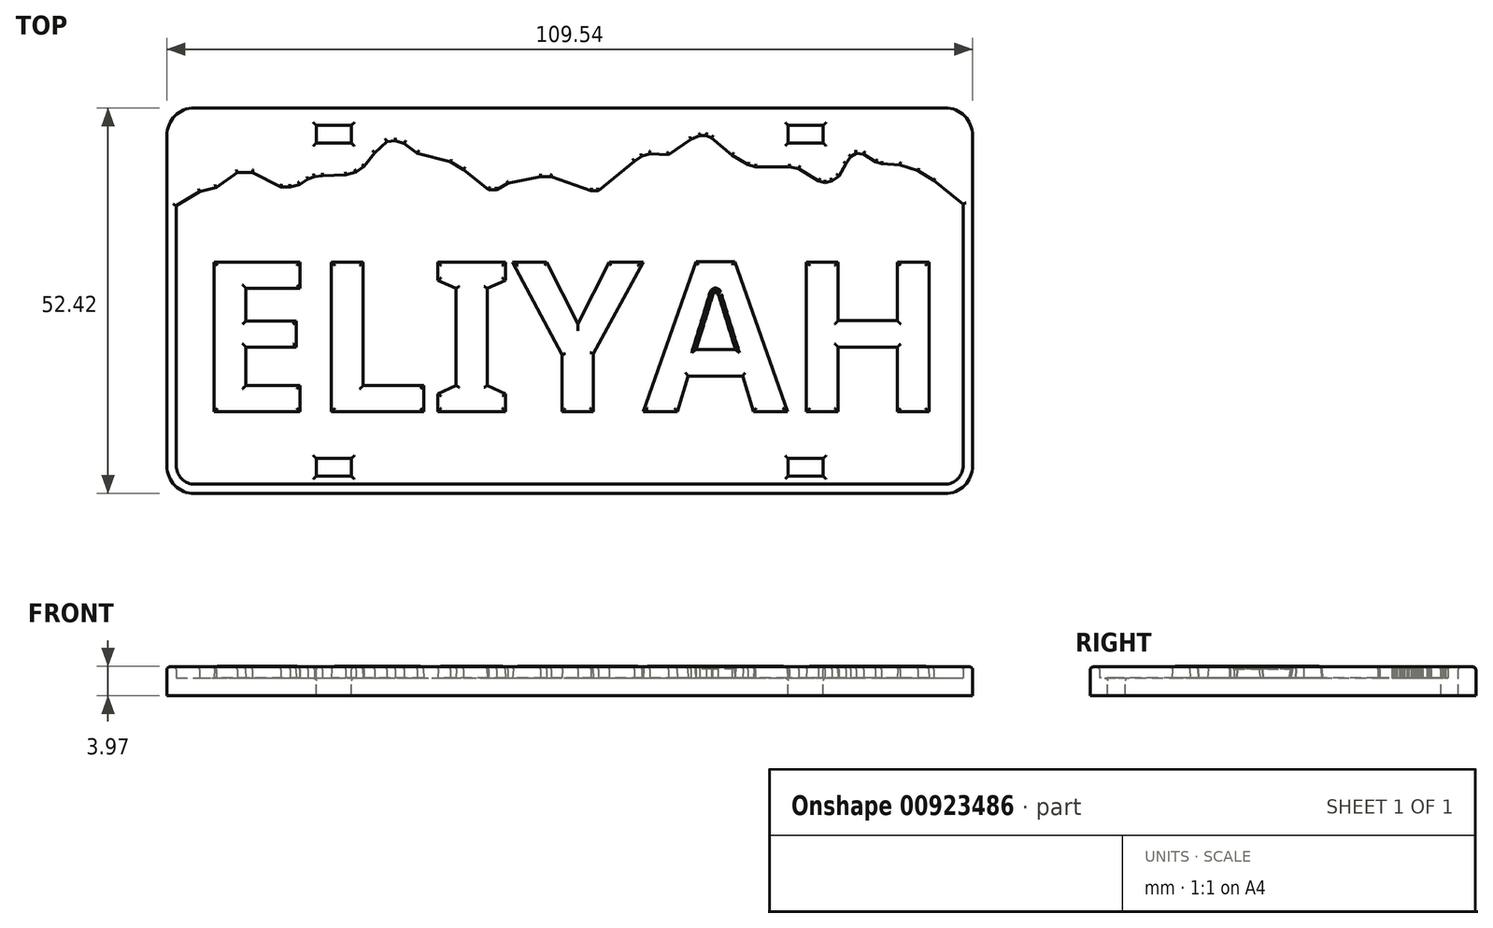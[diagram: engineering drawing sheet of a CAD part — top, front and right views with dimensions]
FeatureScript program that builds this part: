
annotation { "Feature Type Name" : "Feature", "Feature Type Description" : "" }
export const myFeature = defineFeature(function(context is Context, id is Id, definition is map)
    precondition{}
    {
        {
            var Q0;
            Q0=qCreatedBy(makeId("Top.planeOp"),FACE);
            var sketch = newSketch(context, id + "F0", { "sketchPlane" : qUnion([Q0])});
            skLineSegment(sketch, "E0", {"start": v(54.77, -22.46) * mm, "end": v(54.77, 22.46) * mm});
            skArc(sketch, "E1", {"start": v(54.77, 22.46) * mm, "mid": v(53.68, 25.11) * mm, "end": v(51.02, 26.21) * mm});
            skLineSegment(sketch, "E2", {"start": v(51.02, 26.21) * mm, "end": v(-51.02, 26.21) * mm});
            skArc(sketch, "E3", {"start": v(-51.02, 26.21) * mm, "mid": v(-53.68, 25.11) * mm, "end": v(-54.77, 22.46) * mm});
            skLineSegment(sketch, "E4", {"start": v(-54.77, 22.46) * mm, "end": v(-54.77, -22.46) * mm});
            skArc(sketch, "E5", {"start": v(-54.77, -22.46) * mm, "mid": v(-53.54, -25.24) * mm, "end": v(-50.64, -26.2) * mm});
            skLineSegment(sketch, "E6", {"start": v(-50.64, -26.2) * mm, "end": v(51.04, -26.2) * mm});
            skArc(sketch, "E7", {"start": v(51.02, -26.21) * mm, "mid": v(53.68, -25.11) * mm, "end": v(54.77, -22.46) * mm});
            skLineSegment(sketch, "E8", {"start": v(-54.77, 12.13) * mm, "end": v(-50.31, 14.84) * mm});
            skLineSegment(sketch, "E9", {"start": v(-50.31, 14.84) * mm, "end": v(-48.06, 15.4) * mm});
            skLineSegment(sketch, "E10", {"start": v(-48.06, 15.4) * mm, "end": v(-45.2, 17.44) * mm});
            skLineSegment(sketch, "E11", {"start": v(-45.2, 17.44) * mm, "end": v(-43.14, 17.44) * mm});
            skLineSegment(sketch, "E12", {"start": v(-43.14, 17.44) * mm, "end": v(-39.3, 15.5) * mm});
            skLineSegment(sketch, "E13", {"start": v(-39.3, 15.5) * mm, "end": v(-38.03, 15.49) * mm});
            skLineSegment(sketch, "E14", {"start": v(-38.03, 15.49) * mm, "end": v(-36.75, 15.8) * mm});
            skLineSegment(sketch, "E15", {"start": v(-36.75, 15.8) * mm, "end": v(-35.57, 16.54) * mm});
            skLineSegment(sketch, "E16", {"start": v(-35.57, 16.54) * mm, "end": v(-34.73, 16.88) * mm});
            skLineSegment(sketch, "E17", {"start": v(-34.73, 16.88) * mm, "end": v(-33.6, 17.01) * mm});
            skLineSegment(sketch, "E18", {"start": v(-33.6, 17.01) * mm, "end": v(-30.43, 17.11) * mm});
            skLineSegment(sketch, "E19", {"start": v(-29.05, 17.5) * mm, "end": v(-27.98, 18.27) * mm});
            skLineSegment(sketch, "E20", {"start": v(-27.98, 18.27) * mm, "end": v(-26.53, 20.14) * mm});
            skLineSegment(sketch, "E21", {"start": v(-26.53, 20.14) * mm, "end": v(-24.88, 21.63) * mm});
            skLineSegment(sketch, "E22", {"start": v(-24.88, 21.63) * mm, "end": v(-23.73, 21.77) * mm});
            skLineSegment(sketch, "E23", {"start": v(-22.5, 21.4) * mm, "end": v(-20.72, 20.04) * mm});
            skLineSegment(sketch, "E24", {"start": v(-16.23, 18.87) * mm, "end": v(-14.45, 17.85) * mm});
            skLineSegment(sketch, "E25", {"start": v(-14.45, 17.85) * mm, "end": v(-11.02, 15.1) * mm});
            skLineSegment(sketch, "E26", {"start": v(-11.02, 15.1) * mm, "end": v(-9.93, 15.1) * mm});
            skLineSegment(sketch, "E27", {"start": v(-9.93, 15.1) * mm, "end": v(-8.4, 15.96) * mm});
            skLineSegment(sketch, "E28", {"start": v(-8.4, 15.96) * mm, "end": v(-3.94, 16.85) * mm});
            skLineSegment(sketch, "E29", {"start": v(-3.94, 16.85) * mm, "end": v(-2.54, 16.85) * mm});
            skLineSegment(sketch, "E30", {"start": v(-2.54, 16.85) * mm, "end": v(2.9, 14.97) * mm});
            skLineSegment(sketch, "E31", {"start": v(2.9, 14.97) * mm, "end": v(3.92, 14.97) * mm});
            skLineSegment(sketch, "E32", {"start": v(3.92, 14.97) * mm, "end": v(8.8, 18.97) * mm});
            skLineSegment(sketch, "E33", {"start": v(8.8, 18.97) * mm, "end": v(9.82, 19.64) * mm});
            skLineSegment(sketch, "E34", {"start": v(9.82, 19.64) * mm, "end": v(10.9, 19.97) * mm});
            skLineSegment(sketch, "E35", {"start": v(10.9, 19.97) * mm, "end": v(13.43, 19.86) * mm});
            skLineSegment(sketch, "E36", {"start": v(16.5, 21.96) * mm, "end": v(17.71, 22.42) * mm});
            skLineSegment(sketch, "E37", {"start": v(17.71, 22.42) * mm, "end": v(18.56, 22.45) * mm});
            skLineSegment(sketch, "E38", {"start": v(18.56, 22.45) * mm, "end": v(19.28, 22.13) * mm});
            skLineSegment(sketch, "E39", {"start": v(19.28, 22.13) * mm, "end": v(22.05, 19.8) * mm});
            skLineSegment(sketch, "E40", {"start": v(22.05, 19.8) * mm, "end": v(24.2, 18.5) * mm});
            skLineSegment(sketch, "E41", {"start": v(24.2, 18.5) * mm, "end": v(25.23, 18.2) * mm});
            skLineSegment(sketch, "E42", {"start": v(25.23, 18.2) * mm, "end": v(29.85, 18.2) * mm});
            skLineSegment(sketch, "E43", {"start": v(29.85, 18.2) * mm, "end": v(31.13, 17.95) * mm});
            skLineSegment(sketch, "E44", {"start": v(31.13, 17.95) * mm, "end": v(33.84, 16.27) * mm});
            skLineSegment(sketch, "E45", {"start": v(33.84, 16.27) * mm, "end": v(34.73, 16.06) * mm});
            skLineSegment(sketch, "E46", {"start": v(34.73, 16.06) * mm, "end": v(35.67, 16.3) * mm});
            skLineSegment(sketch, "E47", {"start": v(35.67, 16.3) * mm, "end": v(36.58, 16.95) * mm});
            skLineSegment(sketch, "E48", {"start": v(36.58, 16.95) * mm, "end": v(37.58, 18.67) * mm});
            skLineSegment(sketch, "E49", {"start": v(38.22, 19.58) * mm, "end": v(38.96, 20.06) * mm});
            skLineSegment(sketch, "E50", {"start": v(38.96, 20.06) * mm, "end": v(39.94, 19.92) * mm});
            skLineSegment(sketch, "E51", {"start": v(41.58, 18.88) * mm, "end": v(42.4, 18.61) * mm});
            skLineSegment(sketch, "E52", {"start": v(42.4, 18.61) * mm, "end": v(44.9, 18.47) * mm});
            skLineSegment(sketch, "E53", {"start": v(44.9, 18.47) * mm, "end": v(47.31, 17.68) * mm});
            skLineSegment(sketch, "E54", {"start": v(47.31, 17.68) * mm, "end": v(49.47, 16.33) * mm});
            skLineSegment(sketch, "E55", {"start": v(49.47, 16.33) * mm, "end": v(51.88, 14.42) * mm});
            skLineSegment(sketch, "E56", {"start": v(51.88, 14.42) * mm, "end": v(53.78, 12.92) * mm});
            skLineSegment(sketch, "E57", {"start": v(53.78, 12.92) * mm, "end": v(54.77, 12.06) * mm});
            skLineSegment(sketch, "E58", {"start": v(-20.72, 20.04) * mm, "end": v(-16.23, 18.87) * mm});
            skLineSegment(sketch, "E59", {"start": v(16.5, 21.96) * mm, "end": v(13.43, 19.86) * mm});
            skLineSegment(sketch, "E60", {"start": v(-22.5, 21.4) * mm, "end": v(-23.73, 21.77) * mm});
            skLineSegment(sketch, "E61", {"start": v(-29.05, 17.5) * mm, "end": v(-30.43, 17.11) * mm});
            skLineSegment(sketch, "E62", {"start": v(37.58, 18.67) * mm, "end": v(38.22, 19.58) * mm});
            skLineSegment(sketch, "E63", {"start": v(41.58, 18.88) * mm, "end": v(39.94, 19.92) * mm});
            skSolve(sketch);
        }
        {
            var Q0;
            Q0=qCreatedBy(makeId("Top.planeOp"),FACE);
            var sketch = newSketch(context, id + "F1", { "sketchPlane" : qUnion([Q0])});
            skLineSegment(sketch, "E64", {"start": v(54.77, -22.46) * mm, "end": v(54.77, 22.46) * mm});
            skArc(sketch, "E65", {"start": v(54.77, 22.46) * mm, "mid": v(53.68, 25.11) * mm, "end": v(51.02, 26.21) * mm});
            skLineSegment(sketch, "E66", {"start": v(51.02, 26.21) * mm, "end": v(-51.02, 26.21) * mm});
            skArc(sketch, "E67", {"start": v(-51.02, 26.21) * mm, "mid": v(-53.68, 25.11) * mm, "end": v(-54.77, 22.46) * mm});
            skLineSegment(sketch, "E68", {"start": v(-54.77, 22.46) * mm, "end": v(-54.77, -22.46) * mm});
            skArc(sketch, "E69", {"start": v(-54.77, -22.46) * mm, "mid": v(-53.68, -25.11) * mm, "end": v(-51.02, -26.21) * mm});
            skLineSegment(sketch, "E70", {"start": v(-51.02, -26.21) * mm, "end": v(51.02, -26.21) * mm});
            skArc(sketch, "E71", {"start": v(51.02, -26.21) * mm, "mid": v(53.68, -25.11) * mm, "end": v(54.77, -22.46) * mm});
            skLineSegment(sketch, "E72.0", {"start": v(50.96, 24.94) * mm, "end": v(-50.96, 24.94) * mm, "construction": true});
            skLineSegment(sketch, "E72.1", {"start": v(53.5, -22.4) * mm, "end": v(53.5, 22.4) * mm, "construction": true});
            skLineSegment(sketch, "E72.2", {"start": v(-50.96, -24.94) * mm, "end": v(50.96, -24.94) * mm, "construction": true});
            skLineSegment(sketch, "E72.3", {"start": v(-53.5, 22.4) * mm, "end": v(-53.5, -22.4) * mm, "construction": true});
            skPoint(sketch, "E73.visualSharp", {"position": v(-53.5, 24.94) * mm});
            skArc(sketch, "E73.filletArc", {"start": v(-50.96, 24.94) * mm, "mid": v(-52.76, 24.2) * mm, "end": v(-53.5, 22.4) * mm, "construction": true});
            skPoint(sketch, "E74.visualSharp", {"position": v(-53.5, -24.94) * mm});
            skArc(sketch, "E74.filletArc", {"start": v(-53.5, -22.4) * mm, "mid": v(-52.76, -24.2) * mm, "end": v(-50.96, -24.94) * mm, "construction": true});
            skPoint(sketch, "E75.visualSharp", {"position": v(53.5, -24.94) * mm});
            skArc(sketch, "E75.filletArc", {"start": v(50.96, -24.94) * mm, "mid": v(52.76, -24.2) * mm, "end": v(53.5, -22.4) * mm, "construction": true});
            skPoint(sketch, "E76.visualSharp", {"position": v(53.5, 24.94) * mm});
            skArc(sketch, "E76.filletArc", {"start": v(53.5, 22.4) * mm, "mid": v(52.76, 24.2) * mm, "end": v(50.96, 24.94) * mm, "construction": true});
            skSolve(sketch);
        }
        {
            var Q0;
            {var subQ3=sQuery(id+"F0.wireOp",EDGE,"E1");Q0=makeQuery(id+"F0.imprint","IMPRINT",FACE,{"disambiguationData":[TD([[makeQuery(id+"F0.imprint","IMPRINT",EDGE,{"derivedFrom":subQ3}),1.0]])]});}
            extrude(context, id + "F2", {"entities" : qUnion([Q0]), "depth" : 1.52 * mm, "offsetDistance" : 25.4 * mm});
        }
        {
            var Q0;
            Q0=qSketchRegion(id+"F1",true);
            extrude(context, id + "F3", {"entities" : qUnion([Q0]), "operationType" : NewBodyOperationType.ADD, "oppositeDirection" : true, "depth" : 2.38 * mm, "offsetDistance" : 25.4 * mm});
        }
        {
            var Q0;
            {var subQ58=sQuery(id+"F0.wireOp",EDGE,"E0");var subQ59=sQuery(id+"F1.wireOp",EDGE,"E64");var subQ60=sQuery(id+"F1.wireOp",EDGE,"E65");var subQ61=sQuery(id+"F1.wireOp",EDGE,"E68");var subQ62=sQuery(id+"F1.wireOp",EDGE,"E69");var subQ63=sQuery(id+"F1.wireOp",EDGE,"E70");var subQ64=sQuery(id+"F1.wireOp",EDGE,"E71");Q0=makeQuery(id+"F3.boolean.opBoolean","SPLIT",FACE,{"disambiguationData":[TD([makeQuery(id+"F2.opExtrude","SWEPT_FACE",FACE,{"disambiguationData":[OSD([subQ58])]})])],"derivedFrom":makeQuery(id+"F3.opExtrude","CAP_FACE",FACE,{"disambiguationData":[OSD([subQ59,subQ60,sQuery(id+"F1.wireOp",EDGE,"E66"),sQuery(id+"F1.wireOp",EDGE,"E67"),subQ61,subQ62,subQ63,subQ64])],"isStart":true})});}
            var sketch = newSketch(context, id + "F4", { "sketchPlane" : qUnion([Q0])});
            skLineSegment(sketch, "E77", {"start": v(54.77, -22.46) * mm, "end": v(54.77, 12.06) * mm});
            skLineSegment(sketch, "E78", {"start": v(-54.77, 12.13) * mm, "end": v(-54.77, -22.46) * mm});
            skArc(sketch, "E79", {"start": v(-54.77, -22.46) * mm, "mid": v(-53.68, -25.11) * mm, "end": v(-51.02, -26.21) * mm});
            skLineSegment(sketch, "E80", {"start": v(-51.02, -26.21) * mm, "end": v(51.02, -26.21) * mm});
            skArc(sketch, "E81", {"start": v(51.02, -26.21) * mm, "mid": v(53.68, -25.11) * mm, "end": v(54.77, -22.46) * mm});
            skLineSegment(sketch, "E82.1", {"start": v(53.5, -22.4) * mm, "end": v(53.5, 13.14) * mm});
            skLineSegment(sketch, "E82.2", {"start": v(-50.96, -24.94) * mm, "end": v(50.96, -24.94) * mm});
            skLineSegment(sketch, "E82.3", {"start": v(-53.5, 12.9) * mm, "end": v(-53.5, -22.4) * mm});
            skPoint(sketch, "E83.visualSharp", {"position": v(-53.5, 24.94) * mm});
            skPoint(sketch, "E84.visualSharp", {"position": v(-53.5, -24.94) * mm});
            skArc(sketch, "E84.filletArc", {"start": v(-53.5, -22.4) * mm, "mid": v(-52.76, -24.2) * mm, "end": v(-50.96, -24.94) * mm});
            skPoint(sketch, "E85.visualSharp", {"position": v(53.5, -24.94) * mm});
            skArc(sketch, "E85.filletArc", {"start": v(50.96, -24.94) * mm, "mid": v(52.76, -24.2) * mm, "end": v(53.5, -22.4) * mm});
            skPoint(sketch, "E86.visualSharp", {"position": v(53.5, 24.94) * mm});
            skLineSegment(sketch, "E87", {"start": v(-54.77, 12.13) * mm, "end": v(-53.5, 12.9) * mm});
            skLineSegment(sketch, "E88", {"start": v(53.5, 13.14) * mm, "end": v(53.78, 12.92) * mm});
            skLineSegment(sketch, "E89", {"start": v(53.78, 12.92) * mm, "end": v(54.77, 12.06) * mm});
            skSolve(sketch);
        }
        {
            var Q0;
            Q0=qSketchRegion(id+"F4",true);
            extrude(context, id + "F5", {"entities" : qUnion([Q0]), "operationType" : NewBodyOperationType.ADD, "depth" : 1.52 * mm, "offsetDistance" : 25.4 * mm});
        }
        {
            var Q0;
            Q0=makeQuery(id+"F5.boolean.opBoolean","MERGE",FACE,{"derivedFrom":[makeQuery(id+"F2.opExtrude","CAP_FACE",FACE,{"disambiguationData":[OSD([sQuery(id+"F0.wireOp",EDGE,"E0"),sQuery(id+"F0.wireOp",EDGE,"E1"),sQuery(id+"F0.wireOp",EDGE,"E2"),sQuery(id+"F0.wireOp",EDGE,"E3"),sQuery(id+"F0.wireOp",EDGE,"E4"),sQuery(id+"F0.wireOp",EDGE,"E8"),sQuery(id+"F0.wireOp",EDGE,"E9"),sQuery(id+"F0.wireOp",EDGE,"E10"),sQuery(id+"F0.wireOp",EDGE,"E11"),sQuery(id+"F0.wireOp",EDGE,"E12"),sQuery(id+"F0.wireOp",EDGE,"E13"),sQuery(id+"F0.wireOp",EDGE,"E14"),sQuery(id+"F0.wireOp",EDGE,"E15"),sQuery(id+"F0.wireOp",EDGE,"E16"),sQuery(id+"F0.wireOp",EDGE,"E17"),sQuery(id+"F0.wireOp",EDGE,"E18"),sQuery(id+"F0.wireOp",EDGE,"7b9f405e-0691-426e-9c9e-a5372cf0836a"),sQuery(id+"F0.wireOp",EDGE,"E19"),sQuery(id+"F0.wireOp",EDGE,"E20"),sQuery(id+"F0.wireOp",EDGE,"E21"),sQuery(id+"F0.wireOp",EDGE,"E22"),sQuery(id+"F0.wireOp",EDGE,"b3dec5b1-662c-4d50-a13c-af7b7760114a"),sQuery(id+"F0.wireOp",EDGE,"E23"),sQuery(id+"F0.wireOp",EDGE,"4d9ee76e-0833-4cdc-b1a8-2d4ce76e6521"),sQuery(id+"F0.wireOp",EDGE,"E24"),sQuery(id+"F0.wireOp",EDGE,"E25"),sQuery(id+"F0.wireOp",EDGE,"E26"),sQuery(id+"F0.wireOp",EDGE,"E27"),sQuery(id+"F0.wireOp",EDGE,"E28"),sQuery(id+"F0.wireOp",EDGE,"E29"),sQuery(id+"F0.wireOp",EDGE,"E30"),sQuery(id+"F0.wireOp",EDGE,"E31"),sQuery(id+"F0.wireOp",EDGE,"E32"),sQuery(id+"F0.wireOp",EDGE,"E33"),sQuery(id+"F0.wireOp",EDGE,"E34"),sQuery(id+"F0.wireOp",EDGE,"E35"),sQuery(id+"F0.wireOp",EDGE,"55551997-bb9e-4b94-90c5-def3cb147476"),sQuery(id+"F0.wireOp",EDGE,"E36"),sQuery(id+"F0.wireOp",EDGE,"E37"),sQuery(id+"F0.wireOp",EDGE,"E38"),sQuery(id+"F0.wireOp",EDGE,"E39"),sQuery(id+"F0.wireOp",EDGE,"E40"),sQuery(id+"F0.wireOp",EDGE,"E41"),sQuery(id+"F0.wireOp",EDGE,"E42"),sQuery(id+"F0.wireOp",EDGE,"E43"),sQuery(id+"F0.wireOp",EDGE,"E44"),sQuery(id+"F0.wireOp",EDGE,"E45"),sQuery(id+"F0.wireOp",EDGE,"E46"),sQuery(id+"F0.wireOp",EDGE,"E47"),sQuery(id+"F0.wireOp",EDGE,"E48"),sQuery(id+"F0.wireOp",EDGE,"513b7cbe-d979-4e22-b277-f3c42ccdbda1"),sQuery(id+"F0.wireOp",EDGE,"E49"),sQuery(id+"F0.wireOp",EDGE,"E50"),sQuery(id+"F0.wireOp",EDGE,"0d842e13-672c-40e3-aae4-28923e78d4e0"),sQuery(id+"F0.wireOp",EDGE,"E51"),sQuery(id+"F0.wireOp",EDGE,"E52"),sQuery(id+"F0.wireOp",EDGE,"E53"),sQuery(id+"F0.wireOp",EDGE,"E54"),sQuery(id+"F0.wireOp",EDGE,"E55"),sQuery(id+"F0.wireOp",EDGE,"E56"),sQuery(id+"F0.wireOp",EDGE,"E57")])],"isStart":false}),makeQuery(id+"F5.opExtrude","CAP_FACE",FACE,{"disambiguationData":[OSD([sQuery(id+"F4.wireOp",EDGE,"E77"),sQuery(id+"F4.wireOp",EDGE,"E78"),sQuery(id+"F4.wireOp",EDGE,"E79"),sQuery(id+"F4.wireOp",EDGE,"E80"),sQuery(id+"F4.wireOp",EDGE,"E81"),sQuery(id+"F4.wireOp",EDGE,"E82.1"),sQuery(id+"F4.wireOp",EDGE,"E82.2"),sQuery(id+"F4.wireOp",EDGE,"E82.3"),sQuery(id+"F4.wireOp",EDGE,"E84.filletArc"),sQuery(id+"F4.wireOp",EDGE,"E85.filletArc"),sQuery(id+"F4.wireOp",EDGE,"E87"),sQuery(id+"F4.wireOp",EDGE,"E88"),sQuery(id+"F4.wireOp",EDGE,"E89")])],"isStart":false})]});
            var sketch = newSketch(context, id + "F6", { "sketchPlane" : qUnion([Q0])});
            skLineSegment(sketch, "E90.bottom", {"start": v(-34.45, 23.83) * mm, "end": v(-29.7, 23.83) * mm});
            skLineSegment(sketch, "E90.top", {"start": v(-34.45, 21.45) * mm, "end": v(-29.7, 21.45) * mm});
            skLineSegment(sketch, "E90.left", {"start": v(-34.45, 23.83) * mm, "end": v(-34.45, 21.45) * mm});
            skLineSegment(sketch, "E90.right", {"start": v(-29.7, 23.83) * mm, "end": v(-29.7, 21.45) * mm});
            skLineSegment(sketch, "E91", {"start": v(0, 26.21) * mm, "end": v(0, -26.21) * mm, "construction": true});
            skLineSegment(sketch, "E92.MirrorCS", {"start": v(34.45, 23.83) * mm, "end": v(34.45, 21.45) * mm});
            skLineSegment(sketch, "E93.MirrorCS", {"start": v(29.7, 23.83) * mm, "end": v(29.7, 21.45) * mm});
            skLineSegment(sketch, "E94.MirrorCS", {"start": v(34.45, 21.45) * mm, "end": v(29.7, 21.45) * mm});
            skLineSegment(sketch, "E95.MirrorCS", {"start": v(34.45, 23.83) * mm, "end": v(29.7, 23.83) * mm});
            skLineSegment(sketch, "E96", {"start": v(0, 0) * mm, "end": v(-59.23, 0) * mm, "construction": true});
            skLineSegment(sketch, "E97", {"start": v(0, 0) * mm, "end": v(56.47, 0) * mm, "construction": true});
            skLineSegment(sketch, "E98.MirrorCS", {"start": v(-34.45, -23.83) * mm, "end": v(-29.7, -23.83) * mm});
            skLineSegment(sketch, "E99.MirrorCS", {"start": v(-34.45, -23.83) * mm, "end": v(-34.45, -21.45) * mm});
            skLineSegment(sketch, "E100.MirrorCS", {"start": v(-34.45, -21.45) * mm, "end": v(-29.7, -21.45) * mm});
            skLineSegment(sketch, "E101.MirrorCS", {"start": v(-29.7, -23.83) * mm, "end": v(-29.7, -21.45) * mm});
            skLineSegment(sketch, "E102.MirrorCS", {"start": v(29.7, -23.83) * mm, "end": v(29.7, -21.45) * mm});
            skLineSegment(sketch, "E103.MirrorCS", {"start": v(34.45, -23.83) * mm, "end": v(29.7, -23.83) * mm});
            skLineSegment(sketch, "E104.MirrorCS", {"start": v(34.45, -23.83) * mm, "end": v(34.45, -21.45) * mm});
            skLineSegment(sketch, "E105.MirrorCS", {"start": v(34.45, -21.45) * mm, "end": v(29.7, -21.45) * mm});
            skSolve(sketch);
        }
        {
            var Q0;
            Q0=qSketchRegion(id+"F6",true);
            extrude(context, id + "F7", {"entities" : qUnion([Q0]), "operationType" : NewBodyOperationType.REMOVE, "endBound" : BoundingType.THROUGH_ALL, "oppositeDirection" : true, "depth" : 25.4 * mm, "offsetDistance" : 25.4 * mm});
        }
        {
            var Q0;
            Q0=makeQuery(id+"F3.opExtrude","CAP_FACE",FACE,{"disambiguationData":[OSD([sQuery(id+"F1.wireOp",EDGE,"E64"),sQuery(id+"F1.wireOp",EDGE,"E65"),sQuery(id+"F1.wireOp",EDGE,"E66"),sQuery(id+"F1.wireOp",EDGE,"E67"),sQuery(id+"F1.wireOp",EDGE,"E68"),sQuery(id+"F1.wireOp",EDGE,"E69"),sQuery(id+"F1.wireOp",EDGE,"E70"),sQuery(id+"F1.wireOp",EDGE,"E71")])],"isStart":true});
            var sketch = newSketch(context, id + "F8", { "sketchPlane" : qUnion([Q0])});
            skText(sketch, "E106", { "text": "ELIYAH", "fontName": "NotoSans-Bold.ttf"});
            const initialGuessF8  = {"E106": [-0.0509, -0.01508, 1, 0, 0.0205]};
            skSetInitialGuess(sketch, initialGuessF8);
            skSolve(sketch);
        }
        {
            var Q0;
            Q0=qSketchRegion(id+"F8",true);
            extrude(context, id + "F9", {"entities" : qUnion([Q0]), "operationType" : NewBodyOperationType.ADD, "depth" : 1.59 * mm, "offsetDistance" : 25.4 * mm, "hasDraft" : true, "draftAngle" : 3 * degree, "draftPullDirection" : true});
        }
        {
            var Q0;
            Q0=makeQuery(id+"F5.boolean.opBoolean","MERGE",FACE,{"derivedFrom":[makeQuery(id+"F2.opExtrude","CAP_FACE",FACE,{"disambiguationData":[OSD([sQuery(id+"F0.wireOp",EDGE,"E0"),sQuery(id+"F0.wireOp",EDGE,"E1"),sQuery(id+"F0.wireOp",EDGE,"E2"),sQuery(id+"F0.wireOp",EDGE,"E3"),sQuery(id+"F0.wireOp",EDGE,"E4"),sQuery(id+"F0.wireOp",EDGE,"E8"),sQuery(id+"F0.wireOp",EDGE,"E9"),sQuery(id+"F0.wireOp",EDGE,"E10"),sQuery(id+"F0.wireOp",EDGE,"E11"),sQuery(id+"F0.wireOp",EDGE,"E12"),sQuery(id+"F0.wireOp",EDGE,"E13"),sQuery(id+"F0.wireOp",EDGE,"E14"),sQuery(id+"F0.wireOp",EDGE,"E15"),sQuery(id+"F0.wireOp",EDGE,"E16"),sQuery(id+"F0.wireOp",EDGE,"E17"),sQuery(id+"F0.wireOp",EDGE,"E18"),sQuery(id+"F0.wireOp",EDGE,"7b9f405e-0691-426e-9c9e-a5372cf0836a"),sQuery(id+"F0.wireOp",EDGE,"E19"),sQuery(id+"F0.wireOp",EDGE,"E20"),sQuery(id+"F0.wireOp",EDGE,"E21"),sQuery(id+"F0.wireOp",EDGE,"E22"),sQuery(id+"F0.wireOp",EDGE,"b3dec5b1-662c-4d50-a13c-af7b7760114a"),sQuery(id+"F0.wireOp",EDGE,"E23"),sQuery(id+"F0.wireOp",EDGE,"4d9ee76e-0833-4cdc-b1a8-2d4ce76e6521"),sQuery(id+"F0.wireOp",EDGE,"E24"),sQuery(id+"F0.wireOp",EDGE,"E25"),sQuery(id+"F0.wireOp",EDGE,"E26"),sQuery(id+"F0.wireOp",EDGE,"E27"),sQuery(id+"F0.wireOp",EDGE,"E28"),sQuery(id+"F0.wireOp",EDGE,"E29"),sQuery(id+"F0.wireOp",EDGE,"E30"),sQuery(id+"F0.wireOp",EDGE,"E31"),sQuery(id+"F0.wireOp",EDGE,"E32"),sQuery(id+"F0.wireOp",EDGE,"E33"),sQuery(id+"F0.wireOp",EDGE,"E34"),sQuery(id+"F0.wireOp",EDGE,"E35"),sQuery(id+"F0.wireOp",EDGE,"55551997-bb9e-4b94-90c5-def3cb147476"),sQuery(id+"F0.wireOp",EDGE,"E36"),sQuery(id+"F0.wireOp",EDGE,"E37"),sQuery(id+"F0.wireOp",EDGE,"E38"),sQuery(id+"F0.wireOp",EDGE,"E39"),sQuery(id+"F0.wireOp",EDGE,"E40"),sQuery(id+"F0.wireOp",EDGE,"E41"),sQuery(id+"F0.wireOp",EDGE,"E42"),sQuery(id+"F0.wireOp",EDGE,"E43"),sQuery(id+"F0.wireOp",EDGE,"E44"),sQuery(id+"F0.wireOp",EDGE,"E45"),sQuery(id+"F0.wireOp",EDGE,"E46"),sQuery(id+"F0.wireOp",EDGE,"E47"),sQuery(id+"F0.wireOp",EDGE,"E48"),sQuery(id+"F0.wireOp",EDGE,"513b7cbe-d979-4e22-b277-f3c42ccdbda1"),sQuery(id+"F0.wireOp",EDGE,"E49"),sQuery(id+"F0.wireOp",EDGE,"E50"),sQuery(id+"F0.wireOp",EDGE,"0d842e13-672c-40e3-aae4-28923e78d4e0"),sQuery(id+"F0.wireOp",EDGE,"E51"),sQuery(id+"F0.wireOp",EDGE,"E52"),sQuery(id+"F0.wireOp",EDGE,"E53"),sQuery(id+"F0.wireOp",EDGE,"E54"),sQuery(id+"F0.wireOp",EDGE,"E55"),sQuery(id+"F0.wireOp",EDGE,"E56"),sQuery(id+"F0.wireOp",EDGE,"E57")])],"isStart":false}),makeQuery(id+"F5.opExtrude","CAP_FACE",FACE,{"disambiguationData":[OSD([sQuery(id+"F4.wireOp",EDGE,"E77"),sQuery(id+"F4.wireOp",EDGE,"E78"),sQuery(id+"F4.wireOp",EDGE,"E79"),sQuery(id+"F4.wireOp",EDGE,"E80"),sQuery(id+"F4.wireOp",EDGE,"E81"),sQuery(id+"F4.wireOp",EDGE,"E82.1"),sQuery(id+"F4.wireOp",EDGE,"E82.2"),sQuery(id+"F4.wireOp",EDGE,"E82.3"),sQuery(id+"F4.wireOp",EDGE,"E84.filletArc"),sQuery(id+"F4.wireOp",EDGE,"E85.filletArc"),sQuery(id+"F4.wireOp",EDGE,"E87"),sQuery(id+"F4.wireOp",EDGE,"E88"),sQuery(id+"F4.wireOp",EDGE,"E89")])],"isStart":false})]});
            var Q1;
            {var subQ0=sQuery(id+"F1.wireOp",EDGE,"E64");var subQ1=sQuery(id+"F1.wireOp",EDGE,"E68");var subQ2=sQuery(id+"F1.wireOp",EDGE,"E69");var subQ3=sQuery(id+"F1.wireOp",EDGE,"E70");var subQ4=sQuery(id+"F1.wireOp",EDGE,"E71");Q1=makeQuery(id+"F7.boolean.opBoolean","INTERSECT",EDGE,{"derivedFrom":[makeQuery(id+"F3.boolean.opBoolean","SPLIT",FACE,{"disambiguationData":[TD([makeQuery(id+"F2.opExtrude","SWEPT_FACE",FACE,{"disambiguationData":[OSD([sQuery(id+"F0.wireOp",EDGE,"E0")])]})])],"derivedFrom":makeQuery(id+"F3.opExtrude","CAP_FACE",FACE,{"disambiguationData":[OSD([subQ0,sQuery(id+"F1.wireOp",EDGE,"E65"),sQuery(id+"F1.wireOp",EDGE,"E66"),sQuery(id+"F1.wireOp",EDGE,"E67"),subQ1,subQ2,subQ3,subQ4])],"isStart":true})}),makeQuery(id+"F7.opExtrude","SWEPT_FACE",FACE,{"disambiguationData":[OSD([sQuery(id+"F6.wireOp",EDGE,"E100.MirrorCS")])]})]});}
            var Q2;
            {var subQ0=sQuery(id+"F1.wireOp",EDGE,"E64");var subQ1=sQuery(id+"F1.wireOp",EDGE,"E68");var subQ2=sQuery(id+"F1.wireOp",EDGE,"E69");var subQ3=sQuery(id+"F1.wireOp",EDGE,"E70");var subQ4=sQuery(id+"F1.wireOp",EDGE,"E71");Q2=makeQuery(id+"F7.boolean.opBoolean","INTERSECT",EDGE,{"derivedFrom":[makeQuery(id+"F3.boolean.opBoolean","SPLIT",FACE,{"disambiguationData":[TD([makeQuery(id+"F2.opExtrude","SWEPT_FACE",FACE,{"disambiguationData":[OSD([sQuery(id+"F0.wireOp",EDGE,"E0")])]})])],"derivedFrom":makeQuery(id+"F3.opExtrude","CAP_FACE",FACE,{"disambiguationData":[OSD([subQ0,sQuery(id+"F1.wireOp",EDGE,"E65"),sQuery(id+"F1.wireOp",EDGE,"E66"),sQuery(id+"F1.wireOp",EDGE,"E67"),subQ1,subQ2,subQ3,subQ4])],"isStart":true})}),makeQuery(id+"F7.opExtrude","SWEPT_FACE",FACE,{"disambiguationData":[OSD([sQuery(id+"F6.wireOp",EDGE,"E99.MirrorCS")])]})]});}
            var Q3;
            {var subQ0=sQuery(id+"F1.wireOp",EDGE,"E64");var subQ1=sQuery(id+"F1.wireOp",EDGE,"E68");var subQ2=sQuery(id+"F1.wireOp",EDGE,"E69");var subQ3=sQuery(id+"F1.wireOp",EDGE,"E70");var subQ4=sQuery(id+"F1.wireOp",EDGE,"E71");Q3=makeQuery(id+"F7.boolean.opBoolean","INTERSECT",EDGE,{"derivedFrom":[makeQuery(id+"F3.boolean.opBoolean","SPLIT",FACE,{"disambiguationData":[TD([makeQuery(id+"F2.opExtrude","SWEPT_FACE",FACE,{"disambiguationData":[OSD([sQuery(id+"F0.wireOp",EDGE,"E0")])]})])],"derivedFrom":makeQuery(id+"F3.opExtrude","CAP_FACE",FACE,{"disambiguationData":[OSD([subQ0,sQuery(id+"F1.wireOp",EDGE,"E65"),sQuery(id+"F1.wireOp",EDGE,"E66"),sQuery(id+"F1.wireOp",EDGE,"E67"),subQ1,subQ2,subQ3,subQ4])],"isStart":true})}),makeQuery(id+"F7.opExtrude","SWEPT_FACE",FACE,{"disambiguationData":[OSD([sQuery(id+"F6.wireOp",EDGE,"E98.MirrorCS")])]})]});}
            var Q4;
            {var subQ0=sQuery(id+"F1.wireOp",EDGE,"E64");var subQ1=sQuery(id+"F1.wireOp",EDGE,"E68");var subQ2=sQuery(id+"F1.wireOp",EDGE,"E69");var subQ3=sQuery(id+"F1.wireOp",EDGE,"E70");var subQ4=sQuery(id+"F1.wireOp",EDGE,"E71");Q4=makeQuery(id+"F7.boolean.opBoolean","INTERSECT",EDGE,{"derivedFrom":[makeQuery(id+"F3.boolean.opBoolean","SPLIT",FACE,{"disambiguationData":[TD([makeQuery(id+"F2.opExtrude","SWEPT_FACE",FACE,{"disambiguationData":[OSD([sQuery(id+"F0.wireOp",EDGE,"E0")])]})])],"derivedFrom":makeQuery(id+"F3.opExtrude","CAP_FACE",FACE,{"disambiguationData":[OSD([subQ0,sQuery(id+"F1.wireOp",EDGE,"E65"),sQuery(id+"F1.wireOp",EDGE,"E66"),sQuery(id+"F1.wireOp",EDGE,"E67"),subQ1,subQ2,subQ3,subQ4])],"isStart":true})}),makeQuery(id+"F7.opExtrude","SWEPT_FACE",FACE,{"disambiguationData":[OSD([sQuery(id+"F6.wireOp",EDGE,"E101.MirrorCS")])]})]});}
            var Q5;
            {var subQ0=sQuery(id+"F1.wireOp",EDGE,"E64");var subQ1=sQuery(id+"F1.wireOp",EDGE,"E68");var subQ2=sQuery(id+"F1.wireOp",EDGE,"E69");var subQ3=sQuery(id+"F1.wireOp",EDGE,"E70");var subQ4=sQuery(id+"F1.wireOp",EDGE,"E71");Q5=makeQuery(id+"F7.boolean.opBoolean","INTERSECT",EDGE,{"derivedFrom":[makeQuery(id+"F3.boolean.opBoolean","SPLIT",FACE,{"disambiguationData":[TD([makeQuery(id+"F2.opExtrude","SWEPT_FACE",FACE,{"disambiguationData":[OSD([sQuery(id+"F0.wireOp",EDGE,"E0")])]})])],"derivedFrom":makeQuery(id+"F3.opExtrude","CAP_FACE",FACE,{"disambiguationData":[OSD([subQ0,sQuery(id+"F1.wireOp",EDGE,"E65"),sQuery(id+"F1.wireOp",EDGE,"E66"),sQuery(id+"F1.wireOp",EDGE,"E67"),subQ1,subQ2,subQ3,subQ4])],"isStart":true})}),makeQuery(id+"F7.opExtrude","SWEPT_FACE",FACE,{"disambiguationData":[OSD([sQuery(id+"F6.wireOp",EDGE,"E102.MirrorCS")])]})]});}
            var Q6;
            {var subQ0=sQuery(id+"F1.wireOp",EDGE,"E64");var subQ1=sQuery(id+"F1.wireOp",EDGE,"E68");var subQ2=sQuery(id+"F1.wireOp",EDGE,"E69");var subQ3=sQuery(id+"F1.wireOp",EDGE,"E70");var subQ4=sQuery(id+"F1.wireOp",EDGE,"E71");Q6=makeQuery(id+"F7.boolean.opBoolean","INTERSECT",EDGE,{"derivedFrom":[makeQuery(id+"F3.boolean.opBoolean","SPLIT",FACE,{"disambiguationData":[TD([makeQuery(id+"F2.opExtrude","SWEPT_FACE",FACE,{"disambiguationData":[OSD([sQuery(id+"F0.wireOp",EDGE,"E0")])]})])],"derivedFrom":makeQuery(id+"F3.opExtrude","CAP_FACE",FACE,{"disambiguationData":[OSD([subQ0,sQuery(id+"F1.wireOp",EDGE,"E65"),sQuery(id+"F1.wireOp",EDGE,"E66"),sQuery(id+"F1.wireOp",EDGE,"E67"),subQ1,subQ2,subQ3,subQ4])],"isStart":true})}),makeQuery(id+"F7.opExtrude","SWEPT_FACE",FACE,{"disambiguationData":[OSD([sQuery(id+"F6.wireOp",EDGE,"E105.MirrorCS")])]})]});}
            var Q7;
            {var subQ0=sQuery(id+"F1.wireOp",EDGE,"E64");var subQ1=sQuery(id+"F1.wireOp",EDGE,"E68");var subQ2=sQuery(id+"F1.wireOp",EDGE,"E69");var subQ3=sQuery(id+"F1.wireOp",EDGE,"E70");var subQ4=sQuery(id+"F1.wireOp",EDGE,"E71");Q7=makeQuery(id+"F7.boolean.opBoolean","INTERSECT",EDGE,{"derivedFrom":[makeQuery(id+"F3.boolean.opBoolean","SPLIT",FACE,{"disambiguationData":[TD([makeQuery(id+"F2.opExtrude","SWEPT_FACE",FACE,{"disambiguationData":[OSD([sQuery(id+"F0.wireOp",EDGE,"E0")])]})])],"derivedFrom":makeQuery(id+"F3.opExtrude","CAP_FACE",FACE,{"disambiguationData":[OSD([subQ0,sQuery(id+"F1.wireOp",EDGE,"E65"),sQuery(id+"F1.wireOp",EDGE,"E66"),sQuery(id+"F1.wireOp",EDGE,"E67"),subQ1,subQ2,subQ3,subQ4])],"isStart":true})}),makeQuery(id+"F7.opExtrude","SWEPT_FACE",FACE,{"disambiguationData":[OSD([sQuery(id+"F6.wireOp",EDGE,"E104.MirrorCS")])]})]});}
            var Q8;
            {var subQ0=sQuery(id+"F1.wireOp",EDGE,"E64");var subQ1=sQuery(id+"F1.wireOp",EDGE,"E68");var subQ2=sQuery(id+"F1.wireOp",EDGE,"E69");var subQ3=sQuery(id+"F1.wireOp",EDGE,"E70");var subQ4=sQuery(id+"F1.wireOp",EDGE,"E71");Q8=makeQuery(id+"F7.boolean.opBoolean","INTERSECT",EDGE,{"derivedFrom":[makeQuery(id+"F3.boolean.opBoolean","SPLIT",FACE,{"disambiguationData":[TD([makeQuery(id+"F2.opExtrude","SWEPT_FACE",FACE,{"disambiguationData":[OSD([sQuery(id+"F0.wireOp",EDGE,"E0")])]})])],"derivedFrom":makeQuery(id+"F3.opExtrude","CAP_FACE",FACE,{"disambiguationData":[OSD([subQ0,sQuery(id+"F1.wireOp",EDGE,"E65"),sQuery(id+"F1.wireOp",EDGE,"E66"),sQuery(id+"F1.wireOp",EDGE,"E67"),subQ1,subQ2,subQ3,subQ4])],"isStart":true})}),makeQuery(id+"F7.opExtrude","SWEPT_FACE",FACE,{"disambiguationData":[OSD([sQuery(id+"F6.wireOp",EDGE,"E103.MirrorCS")])]})]});}
            var Q9;
            Q9=makeQuery(id+"F9.opExtrude","CAP_FACE",FACE,{"disambiguationData":[OSD([sQuery(id+"F8.wireOp",EDGE,"E106.sketch_text.stroke-0"),sQuery(id+"F8.wireOp",EDGE,"E106.sketch_text.stroke-1"),sQuery(id+"F8.wireOp",EDGE,"E106.sketch_text.stroke-2"),sQuery(id+"F8.wireOp",EDGE,"E106.sketch_text.stroke-3"),sQuery(id+"F8.wireOp",EDGE,"E106.sketch_text.stroke-4"),sQuery(id+"F8.wireOp",EDGE,"E106.sketch_text.stroke-5"),sQuery(id+"F8.wireOp",EDGE,"E106.sketch_text.stroke-6"),sQuery(id+"F8.wireOp",EDGE,"E106.sketch_text.stroke-7"),sQuery(id+"F8.wireOp",EDGE,"E106.sketch_text.stroke-8"),sQuery(id+"F8.wireOp",EDGE,"E106.sketch_text.stroke-9"),sQuery(id+"F8.wireOp",EDGE,"E106.sketch_text.stroke-10"),sQuery(id+"F8.wireOp",EDGE,"E106.sketch_text.stroke-11"),sQuery(id+"F8.wireOp",EDGE,"E106.sketch_text.stroke-12"),sQuery(id+"F8.wireOp",EDGE,"E106.sketch_text.stroke-13"),sQuery(id+"F8.wireOp",EDGE,"E106.sketch_text.stroke-14")])],"isStart":false});
            var Q10;
            Q10=makeQuery(id+"F9.opExtrude","CAP_FACE",FACE,{"disambiguationData":[OSD([sQuery(id+"F8.wireOp",EDGE,"E106.sketch_text.stroke-15"),sQuery(id+"F8.wireOp",EDGE,"E106.sketch_text.stroke-16"),sQuery(id+"F8.wireOp",EDGE,"E106.sketch_text.stroke-17"),sQuery(id+"F8.wireOp",EDGE,"E106.sketch_text.stroke-18"),sQuery(id+"F8.wireOp",EDGE,"E106.sketch_text.stroke-19"),sQuery(id+"F8.wireOp",EDGE,"E106.sketch_text.stroke-20"),sQuery(id+"F8.wireOp",EDGE,"E106.sketch_text.stroke-21"),sQuery(id+"F8.wireOp",EDGE,"E106.sketch_text.stroke-22"),sQuery(id+"F8.wireOp",EDGE,"E106.sketch_text.stroke-23"),sQuery(id+"F8.wireOp",EDGE,"E106.sketch_text.stroke-24"),sQuery(id+"F8.wireOp",EDGE,"E106.sketch_text.stroke-25"),sQuery(id+"F8.wireOp",EDGE,"E106.sketch_text.stroke-26"),sQuery(id+"F8.wireOp",EDGE,"E106.sketch_text.stroke-27"),sQuery(id+"F8.wireOp",EDGE,"E106.sketch_text.stroke-28")])],"isStart":false});
            var Q11;
            Q11=makeQuery(id+"F9.opExtrude","CAP_FACE",FACE,{"disambiguationData":[OSD([sQuery(id+"F8.wireOp",EDGE,"E106.sketch_text.stroke-29"),sQuery(id+"F8.wireOp",EDGE,"E106.sketch_text.stroke-30"),sQuery(id+"F8.wireOp",EDGE,"E106.sketch_text.stroke-31"),sQuery(id+"F8.wireOp",EDGE,"E106.sketch_text.stroke-32"),sQuery(id+"F8.wireOp",EDGE,"E106.sketch_text.stroke-33"),sQuery(id+"F8.wireOp",EDGE,"E106.sketch_text.stroke-34"),sQuery(id+"F8.wireOp",EDGE,"E106.sketch_text.stroke-35"),sQuery(id+"F8.wireOp",EDGE,"E106.sketch_text.stroke-36"),sQuery(id+"F8.wireOp",EDGE,"E106.sketch_text.stroke-37"),sQuery(id+"F8.wireOp",EDGE,"E106.sketch_text.stroke-38"),sQuery(id+"F8.wireOp",EDGE,"E106.sketch_text.stroke-39"),sQuery(id+"F8.wireOp",EDGE,"E106.sketch_text.stroke-40"),sQuery(id+"F8.wireOp",EDGE,"E106.sketch_text.stroke-41"),sQuery(id+"F8.wireOp",EDGE,"E106.sketch_text.stroke-42")])],"isStart":false});
            var Q12;
            Q12=makeQuery(id+"F9.opExtrude","CAP_FACE",FACE,{"disambiguationData":[OSD([sQuery(id+"F8.wireOp",EDGE,"E106.sketch_text.stroke-57"),sQuery(id+"F8.wireOp",EDGE,"E106.sketch_text.stroke-58"),sQuery(id+"F8.wireOp",EDGE,"E106.sketch_text.stroke-59"),sQuery(id+"F8.wireOp",EDGE,"E106.sketch_text.stroke-60"),sQuery(id+"F8.wireOp",EDGE,"E106.sketch_text.stroke-61"),sQuery(id+"F8.wireOp",EDGE,"E106.sketch_text.stroke-62"),sQuery(id+"F8.wireOp",EDGE,"E106.sketch_text.stroke-63"),sQuery(id+"F8.wireOp",EDGE,"E106.sketch_text.stroke-64"),sQuery(id+"F8.wireOp",EDGE,"E106.sketch_text.stroke-65"),sQuery(id+"F8.wireOp",EDGE,"E106.sketch_text.stroke-66"),sQuery(id+"F8.wireOp",EDGE,"E106.sketch_text.stroke-67"),sQuery(id+"F8.wireOp",EDGE,"E106.sketch_text.stroke-68"),sQuery(id+"F8.wireOp",EDGE,"E106.sketch_text.stroke-69"),sQuery(id+"F8.wireOp",EDGE,"E106.sketch_text.stroke-70")])],"isStart":false});
            var Q13;
            Q13=makeQuery(id+"F9.opExtrude","CAP_FACE",FACE,{"disambiguationData":[OSD([sQuery(id+"F8.wireOp",EDGE,"E106.sketch_text.stroke-71"),sQuery(id+"F8.wireOp",EDGE,"E106.sketch_text.stroke-72"),sQuery(id+"F8.wireOp",EDGE,"E106.sketch_text.stroke-73"),sQuery(id+"F8.wireOp",EDGE,"E106.sketch_text.stroke-74"),sQuery(id+"F8.wireOp",EDGE,"E106.sketch_text.stroke-75"),sQuery(id+"F8.wireOp",EDGE,"E106.sketch_text.stroke-76"),sQuery(id+"F8.wireOp",EDGE,"E106.sketch_text.stroke-77"),sQuery(id+"F8.wireOp",EDGE,"E106.sketch_text.stroke-78"),sQuery(id+"F8.wireOp",EDGE,"E106.sketch_text.stroke-79"),sQuery(id+"F8.wireOp",EDGE,"E106.sketch_text.stroke-80"),sQuery(id+"F8.wireOp",EDGE,"E106.sketch_text.stroke-81"),sQuery(id+"F8.wireOp",EDGE,"E106.sketch_text.stroke-82"),sQuery(id+"F8.wireOp",EDGE,"E106.sketch_text.stroke-83"),sQuery(id+"F8.wireOp",EDGE,"E106.sketch_text.stroke-84"),sQuery(id+"F8.wireOp",EDGE,"E106.sketch_text.stroke-85"),sQuery(id+"F8.wireOp",EDGE,"E106.sketch_text.stroke-86"),sQuery(id+"F8.wireOp",EDGE,"E106.sketch_text.stroke-87"),sQuery(id+"F8.wireOp",EDGE,"E106.sketch_text.stroke-88"),sQuery(id+"F8.wireOp",EDGE,"E106.sketch_text.stroke-89")])],"isStart":false});
            var Q14;
            Q14=makeQuery(id+"F9.opExtrude","CAP_FACE",FACE,{"disambiguationData":[OSD([sQuery(id+"F8.wireOp",EDGE,"E106.sketch_text.stroke-43"),sQuery(id+"F8.wireOp",EDGE,"E106.sketch_text.stroke-44"),sQuery(id+"F8.wireOp",EDGE,"E106.sketch_text.stroke-45"),sQuery(id+"F8.wireOp",EDGE,"E106.sketch_text.stroke-46"),sQuery(id+"F8.wireOp",EDGE,"E106.sketch_text.stroke-47"),sQuery(id+"F8.wireOp",EDGE,"E106.sketch_text.stroke-48"),sQuery(id+"F8.wireOp",EDGE,"E106.sketch_text.stroke-49"),sQuery(id+"F8.wireOp",EDGE,"E106.sketch_text.stroke-50"),sQuery(id+"F8.wireOp",EDGE,"E106.sketch_text.stroke-51"),sQuery(id+"F8.wireOp",EDGE,"E106.sketch_text.stroke-52"),sQuery(id+"F8.wireOp",EDGE,"E106.sketch_text.stroke-53"),sQuery(id+"F8.wireOp",EDGE,"E106.sketch_text.stroke-54"),sQuery(id+"F8.wireOp",EDGE,"E106.sketch_text.stroke-55"),sQuery(id+"F8.wireOp",EDGE,"E106.sketch_text.stroke-56")])],"isStart":false});
            var Q15;
            Q15=makeQuery(id+"F9.opExtrude","CAP_FACE",FACE,{"disambiguationData":[OSD([sQuery(id+"F8.wireOp",EDGE,"E106.sketch_text.stroke-12"),sQuery(id+"F8.wireOp",EDGE,"E106.sketch_text.stroke-13"),sQuery(id+"F8.wireOp",EDGE,"E106.sketch_text.stroke-14"),sQuery(id+"F8.wireOp",EDGE,"E106.sketch_text.stroke-15"),sQuery(id+"F8.wireOp",EDGE,"E106.sketch_text.stroke-16"),sQuery(id+"F8.wireOp",EDGE,"E106.sketch_text.stroke-17")])],"isStart":false});
            var Q16;
            Q16=makeQuery(id+"F9.opExtrude","SWEPT_EDGE",EDGE,{"disambiguationData":[OSD([sQuery(id+"F8.wireOp",EDGE,"E106.sketch_text.stroke-48"),sQuery(id+"F8.wireOp",EDGE,"E106.sketch_text.stroke-49")])]});
            fillet(context, id + "F10", {"entities" : qUnion([Q0, Q1, Q2, Q3, Q4, Q5, Q6, Q7, Q8, Q9, Q10, Q11, Q12, Q13, Q14, Q15, Q16]), "radius" : 0.38 * mm, "tangentPropagation" : true, "allowEdgeOverflow" : false});
        }
    });
